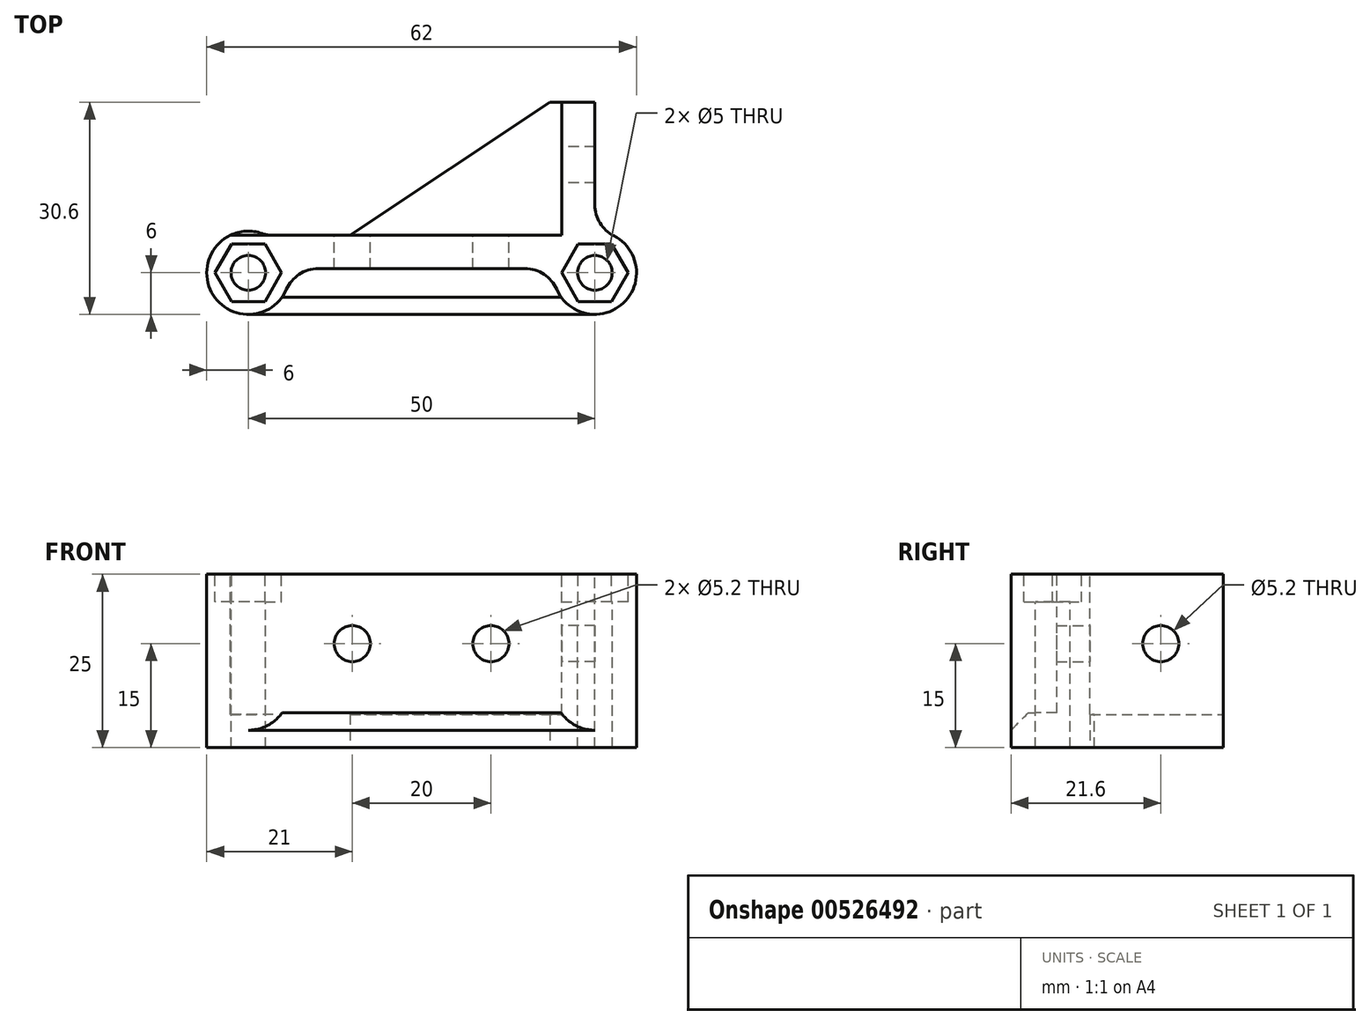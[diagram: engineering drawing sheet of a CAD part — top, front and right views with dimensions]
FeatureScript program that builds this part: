
annotation { "Feature Type Name" : "Feature", "Feature Type Description" : "" }
export const myFeature = defineFeature(function(context is Context, id is Id, definition is map)
    precondition{}
    {
        {
            var Q0;
            Q0=qCreatedBy(makeId("Top.planeOp"),FACE);
            var sketch = newSketch(context, id + "F0", { "sketchPlane" : qUnion([Q0])});
            skCircle(sketch, "E0", {"center": v(-25, 0) * mm, "radius": 2.5 * mm});
            skArc(sketch, "E1", {"start": v(-23.05, 5.67) * mm, "mid": v(-30.5, -2.41) * mm, "end": v(-19.5, -2.4) * mm});
            skCircle(sketch, "E2", {"center": v(25, 0) * mm, "radius": 2.5 * mm});
            skArc(sketch, "E3", {"start": v(19.5, -2.4) * mm, "mid": v(29.11, -4.37) * mm, "end": v(27.73, 5.34) * mm});
            skLineSegment(sketch, "E4", {"start": v(-21.42, 5.4) * mm, "end": v(20.2, 5.4) * mm});
            skLineSegment(sketch, "E5", {"start": v(-14.92, 0.6) * mm, "end": v(14.92, 0.6) * mm});
            skArc(sketch, "E6", {"start": v(-14.92, 0.6) * mm, "mid": v(-17.66, -0.22) * mm, "end": v(-19.5, -2.4) * mm});
            skArc(sketch, "E7", {"start": v(14.92, 0.6) * mm, "mid": v(17.66, -0.22) * mm, "end": v(19.5, -2.4) * mm});
            skLineSegment(sketch, "E8", {"start": v(20.2, 5.4) * mm, "end": v(20.2, 24.6) * mm});
            skLineSegment(sketch, "E9", {"start": v(20.2, 24.6) * mm, "end": v(25, 24.6) * mm});
            skLineSegment(sketch, "E10", {"start": v(25, 24.6) * mm, "end": v(25, 9.8) * mm});
            skArc(sketch, "E11", {"start": v(25, 9.8) * mm, "mid": v(25.74, 7.19) * mm, "end": v(27.73, 5.34) * mm});
            skLineSegment(sketch, "E12", {"start": v(-25, 0) * mm, "end": v(25, 0) * mm, "construction": true});
            skPoint(sketch, "E13.visualSharp", {"position": v(-22.38, 5.4) * mm});
            skArc(sketch, "E13.filletArc", {"start": v(-23.05, 5.67) * mm, "mid": v(-22.24, 5.47) * mm, "end": v(-21.42, 5.4) * mm});
            skSolve(sketch);
        }
        {
            var Q0;
            Q0 = qSketchRegion(id + "F0", true);
            extrude(context, id + "F1", {"entities" : qUnion([Q0]), "oppositeDirection" : true, "depth" : 25 * mm, "offsetDistance" : 25 * mm});
        }
        {
            var Q0;
            Q0=makeQuery(id+"F1.opExtrude","CAP_FACE",FACE,{"disambiguationData":[OSD([sQuery(id+"F0.wireOp",EDGE,"E0"),sQuery(id+"F0.wireOp",EDGE,"E1"),sQuery(id+"F0.wireOp",EDGE,"E2"),sQuery(id+"F0.wireOp",EDGE,"E3"),sQuery(id+"F0.wireOp",EDGE,"E4"),sQuery(id+"F0.wireOp",EDGE,"E5"),sQuery(id+"F0.wireOp",EDGE,"E6"),sQuery(id+"F0.wireOp",EDGE,"E7"),sQuery(id+"F0.wireOp",EDGE,"E8"),sQuery(id+"F0.wireOp",EDGE,"E9"),sQuery(id+"F0.wireOp",EDGE,"E10"),sQuery(id+"F0.wireOp",EDGE,"E11")])],"isStart":true});
            var sketch = newSketch(context, id + "F2", { "sketchPlane" : qUnion([Q0])});
            skCircle(sketch, "E14.cCircle", {"center": v(25, 0) * mm, "radius": 4.16 * mm, "construction": true});
            skLineSegment(sketch, "E14.0", {"start": v(20.2, 0) * mm, "end": v(22.6, 4.16) * mm});
            skLineSegment(sketch, "E14.1", {"start": v(22.6, 4.16) * mm, "end": v(27.4, 4.16) * mm});
            skLineSegment(sketch, "E14.2", {"start": v(27.4, 4.16) * mm, "end": v(29.8, 0) * mm});
            skLineSegment(sketch, "E14.3", {"start": v(29.8, 0) * mm, "end": v(27.4, -4.16) * mm});
            skLineSegment(sketch, "E14.4", {"start": v(27.4, -4.16) * mm, "end": v(22.6, -4.16) * mm});
            skLineSegment(sketch, "E14.5", {"start": v(22.6, -4.16) * mm, "end": v(20.2, 0) * mm});
            skPoint(sketch, "E14.0.midPoint", {"position": v(21.4, 2.08) * mm});
            skLineSegment(sketch, "E15", {"start": v(0, 0.6) * mm, "end": v(0, -5.53) * mm, "construction": true});
            skLineSegment(sketch, "E16.MirrorCS", {"start": v(-27.4, 4.16) * mm, "end": v(-29.8, 0) * mm});
            skLineSegment(sketch, "E17.MirrorCS", {"start": v(-22.6, 4.16) * mm, "end": v(-27.4, 4.16) * mm});
            skLineSegment(sketch, "E18.MirrorCS", {"start": v(-20.2, 0) * mm, "end": v(-22.6, 4.16) * mm});
            skLineSegment(sketch, "E19.MirrorCS", {"start": v(-22.6, -4.16) * mm, "end": v(-20.2, 0) * mm});
            skLineSegment(sketch, "E20.MirrorCS", {"start": v(-27.4, -4.16) * mm, "end": v(-22.6, -4.16) * mm});
            skLineSegment(sketch, "E21.MirrorCS", {"start": v(-29.8, 0) * mm, "end": v(-27.4, -4.16) * mm});
            skSolve(sketch);
        }
        {
            var Q0;
            Q0 = qSketchRegion(id + "F2", true);
            extrude(context, id + "F3", {"entities" : qUnion([Q0]), "operationType" : NewBodyOperationType.REMOVE, "oppositeDirection" : true, "depth" : 4 * mm, "offsetDistance" : 25 * mm});
        }
        {
            var Q0;
            Q0=makeQuery(id+"F1.opExtrude","CAP_FACE",FACE,{"disambiguationData":[OSD([sQuery(id+"F0.wireOp",EDGE,"E0"),sQuery(id+"F0.wireOp",EDGE,"E1"),sQuery(id+"F0.wireOp",EDGE,"E2"),sQuery(id+"F0.wireOp",EDGE,"E3"),sQuery(id+"F0.wireOp",EDGE,"E4"),sQuery(id+"F0.wireOp",EDGE,"E5"),sQuery(id+"F0.wireOp",EDGE,"E6"),sQuery(id+"F0.wireOp",EDGE,"E7"),sQuery(id+"F0.wireOp",EDGE,"E8"),sQuery(id+"F0.wireOp",EDGE,"E9"),sQuery(id+"F0.wireOp",EDGE,"E10"),sQuery(id+"F0.wireOp",EDGE,"E11"),sQuery(id+"F0.wireOp",EDGE,"E13.filletArc")])],"isStart":false});
            var sketch = newSketch(context, id + "F4", { "sketchPlane" : qUnion([Q0])});
            skLineSegment(sketch, "E22", {"start": v(20.2, -24.6) * mm, "end": v(18.5, -24.6) * mm});
            skLineSegment(sketch, "E23", {"start": v(18.5, -24.6) * mm, "end": v(-10.3, -5.4) * mm});
            skLineSegment(sketch, "E24", {"start": v(-10.3, -5.4) * mm, "end": v(20.2, -5.4) * mm});
            skLineSegment(sketch, "E25", {"start": v(20.2, -5.4) * mm, "end": v(20.2, -24.6) * mm});
            skSolve(sketch);
        }
        {
            var Q0;
            Q0 = qSketchRegion(id + "F4", true);
            extrude(context, id + "F5", {"entities" : qUnion([Q0]), "operationType" : NewBodyOperationType.ADD, "oppositeDirection" : true, "depth" : 4.8 * mm, "offsetDistance" : 25 * mm});
        }
        {
            var Q0;
            Q0=makeQuery(id+"F1.opExtrude","SWEPT_FACE",FACE,{"disambiguationData":[OSD([sQuery(id+"F0.wireOp",EDGE,"E4")])]});
            var sketch = newSketch(context, id + "F6", { "sketchPlane" : qUnion([Q0])});
            skCircle(sketch, "E26", {"center": v(-10, -10) * mm, "radius": 2.6 * mm});
            skCircle(sketch, "E27", {"center": v(10, -10) * mm, "radius": 2.6 * mm});
            skLineSegment(sketch, "E28", {"start": v(-10, -10) * mm, "end": v(10, -10) * mm, "construction": true});
            skSolve(sketch);
        }
        {
            var Q0;
            Q0 = qSketchRegion(id + "F6", true);
            extrude(context, id + "F7", {"entities" : qUnion([Q0]), "operationType" : NewBodyOperationType.REMOVE, "endBound" : BoundingType.UP_TO_NEXT, "oppositeDirection" : true, "depth" : 25 * mm, "offsetDistance" : 25 * mm});
        }
        {
            var Q0;
            Q0=makeQuery(id+"F1.opExtrude","SWEPT_FACE",FACE,{"disambiguationData":[OSD([sQuery(id+"F0.wireOp",EDGE,"E8")])]});
            var sketch = newSketch(context, id + "F8", { "sketchPlane" : qUnion([Q0])});
            skLineSegment(sketch, "E29", {"start": v(-24.6, -10) * mm, "end": v(-15.6, -10) * mm, "construction": true});
            skLineSegment(sketch, "E30", {"start": v(-15.6, -10) * mm, "end": v(-15.6, 0) * mm, "construction": true});
            skCircle(sketch, "E31", {"center": v(-15.6, -10) * mm, "radius": 2.6 * mm});
            skSolve(sketch);
        }
        {
            var Q0;
            Q0 = qSketchRegion(id + "F8", true);
            extrude(context, id + "F9", {"entities" : qUnion([Q0]), "operationType" : NewBodyOperationType.REMOVE, "endBound" : BoundingType.UP_TO_NEXT, "oppositeDirection" : true, "depth" : 25 * mm, "offsetDistance" : 25 * mm});
        }
        {
            var Q0;
            Q0=qCreatedBy(makeId("Right.planeOp"),FACE);
            var sketch = newSketch(context, id + "F10", { "sketchPlane" : qUnion([Q0])});
            skLineSegment(sketch, "E32", {"start": v(0.6, -20) * mm, "end": v(0.6, -25) * mm});
            skLineSegment(sketch, "E33", {"start": v(0.6, -25) * mm, "end": v(-6, -25) * mm});
            skLineSegment(sketch, "E34", {"start": v(-6, -25) * mm, "end": v(-6, -22.5) * mm});
            skLineSegment(sketch, "E35", {"start": v(-6, -22.5) * mm, "end": v(-3.5, -20) * mm});
            skLineSegment(sketch, "E36", {"start": v(-3.5, -20) * mm, "end": v(0.6, -20) * mm});
            skPoint(sketch, "E37.orphan", {"position": v(0.6, 0) * mm});
            skLineSegment(sketch, "E38.0.2", {"start": v(-6, -25) * mm, "end": v(5.34, -25) * mm, "construction": true});
            skSolve(sketch);
        }
        {
            var Q0;
            Q0 = qSketchRegion(id + "F10", true);
            extrude(context, id + "F11", {"entities" : qUnion([Q0]), "operationType" : NewBodyOperationType.ADD, "endBound" : BoundingType.UP_TO_NEXT, "depth" : 25 * mm, "offsetDistance" : 25 * mm, "hasSecondDirection" : true, "secondDirectionBound" : BoundingType.UP_TO_NEXT, "secondDirectionOppositeDirection" : true, "secondDirectionDepth" : 25 * mm});
        }
        {
            var Q0;
            Q0=makeQuery(id+"F1.opExtrude","CAP_FACE",FACE,{"disambiguationData":[OSD([sQuery(id+"F0.wireOp",EDGE,"E0"),sQuery(id+"F0.wireOp",EDGE,"E1"),sQuery(id+"F0.wireOp",EDGE,"E2"),sQuery(id+"F0.wireOp",EDGE,"E3"),sQuery(id+"F0.wireOp",EDGE,"E4"),sQuery(id+"F0.wireOp",EDGE,"E5"),sQuery(id+"F0.wireOp",EDGE,"E6"),sQuery(id+"F0.wireOp",EDGE,"E7"),sQuery(id+"F0.wireOp",EDGE,"E8"),sQuery(id+"F0.wireOp",EDGE,"E9"),sQuery(id+"F0.wireOp",EDGE,"E10"),sQuery(id+"F0.wireOp",EDGE,"E11"),sQuery(id+"F0.wireOp",EDGE,"E13.filletArc")])],"isStart":true});
            var sketch = newSketch(context, id + "F12", { "sketchPlane" : qUnion([Q0])});
            skLineSegment(sketch, "E39.bottom", {"start": v(-21.42, 5.4) * mm, "end": v(-27.62, 5.4) * mm});
            skLineSegment(sketch, "E39.top", {"start": v(-21.42, 8.4) * mm, "end": v(-27.62, 8.4) * mm});
            skLineSegment(sketch, "E39.left", {"start": v(-21.42, 5.4) * mm, "end": v(-21.42, 8.4) * mm});
            skLineSegment(sketch, "E39.right", {"start": v(-27.62, 5.4) * mm, "end": v(-27.62, 8.4) * mm});
            skSolve(sketch);
        }
        {
            var Q0;
            Q0 = qSketchRegion(id + "F12", true);
            var Q1;
            Q1=makeQuery(id+"F5.opExtrude","CAP_FACE",FACE,{"disambiguationData":[OSD([sQuery(id+"F4.wireOp",EDGE,"E22"),sQuery(id+"F4.wireOp",EDGE,"E23"),sQuery(id+"F4.wireOp",EDGE,"E24"),sQuery(id+"F4.wireOp",EDGE,"E25")])],"isStart":false});
            extrude(context, id + "F13", {"entities" : qUnion([Q0]), "operationType" : NewBodyOperationType.REMOVE, "endBound" : BoundingType.UP_TO_SURFACE, "oppositeDirection" : true, "depth" : 25 * mm, "endBoundEntityFace" : qUnion([Q1]), "offsetDistance" : 25 * mm});
        }
    });
